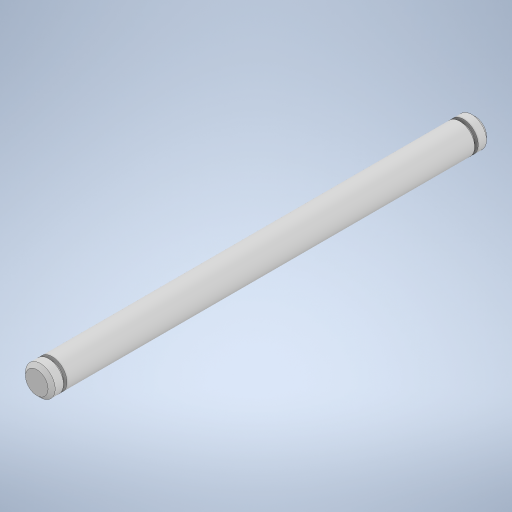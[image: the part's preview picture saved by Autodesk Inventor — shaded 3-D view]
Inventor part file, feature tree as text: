
AUTODESK INVENTOR PART (.ipt)
format: ipt  version: 2024 (Build 280153000, 153)  size: 256,512 bytes
history: native  units: in
note: dims shown in document units (in); Inventor stores cm internally (conversion verified against a paired STEP export)
features: extrude x3, sketch x3, chamfer x1, mirror x1, plane x1
ambient origin geometry x8: Origin, YZ Plane, XZ Plane, XY Plane, X Axis, Y Axis, Z Axis, Center Point
bodies: Solid1 (feature_tree)
feature tree (9):
  extrude  "Extrusion1"  Depth=1.7238in TaperAngle=0.0deg
  extrude  "Extrusion2"  Depth=0.015in TaperAngle=0.0deg
  extrude  "Extrusion3"  Depth=0.05in TaperAngle=0.0deg
  chamfer  "Chamfer1"  Distance=0.015in Angle=45.0deg
  mirror  "Mirror1"
  sketch  "Sketch1"  dims[d0=0.125in d1=1.7238in d2=0.0in]
  sketch  "Sketch2"  dims[d3=0.0938in d4=0.015in d5=0.0in]
  sketch  "Sketch3"  dims[d6=0.125in d7=0.05in d8=0.0in d9=0.015in d10=0.125in d11=45.0deg]
  plane  "Work Plane1"
